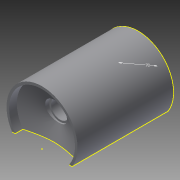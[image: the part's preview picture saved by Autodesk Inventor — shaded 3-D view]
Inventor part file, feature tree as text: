
AUTODESK INVENTOR PART (.ipt)
format: ipt  version: 2014 (Build 180170000, 170)  size: 152,064 bytes
history: native  units: mm
features: sketch x7, extrude x3, plane x2, chamfer x1, loft x1, projected_geometry x1
ambient origin geometry x8: Origin, YZ Plane, XZ Plane, XY Plane, X Axis, Y Axis, Z Axis, Center Point
bodies: Solid1 (feature_tree)
feature tree (15):
  extrude  "Extrusion1"  Depth=45.0mm
  sketch  "Sketch2"  dims[d2=55.0mm d3=5.0mm]
  plane  "Work Plane1"
  extrude  "Extrusion2"  Depth=55.0mm
  chamfer  "Chamfer1"  Distance=160.0mm
  sketch  "Sketch4"  dims[d7=70.0mm d8=-30.0mm]
  sketch  "Sketch5"  dims[d9=19.0mm d10=0.0mm d11=55.0mm d12=17.0mm d13=45.0deg]
  plane  "Work Plane2"
  extrude  "Extrusion3"  [1 undecoded]
  loft  "Loft1"
  sketch  "Sketch1"  dims[d0=90.0mm d1=45.0mm]
  sketch  "Sketch3"  dims[d4=5.0mm d5=160.0mm d6=0.0mm]
  projected_geometry  "Projected Loop1"
  sketch  "Sketch6"  dims[d14=33.0mm]
  sketch  "Sketch7"  dims[d15=-19.0mm d16=36.0mm d17=27.0mm d18=0.0mm d19=30.0mm d20=0.0mm d21=90.0deg d22=0.0mm d23=90.0deg]
note: 1 required parameter value undecoded (feature->parameter linkage not recoverable at this tier; creation-order binding heuristic only, values carry confidence <= 0.55)
